# Revit family: SAS-6001_GENERADO
name_source: partatom
category: Equipos mecánicos
revit_build: Autodesk Revit 2014 (Build: 20130308_1515(x64)
units: mm (PartAtom-declared; Revit-internal decimal feet)

## types (10) — shared parameters
Depth = 693 mm  [stored 2.27362 ft]
Fabricante = SAMMIC S.L.
Foodservice Equipment Identifier = Sí
HP = 1.61
Height = 783 mm  [stored 2.5689 ft]
Revision Code = 1
URL = https://www.sammic.com
URL Cutsheet = http://www.sammic.com
Watts = 1200 W
Weight in Pounds = 286.6
Width = 630 mm  [stored 2.06693 ft]

## per-type parameters (varying)
| type | Comentarios de tipo | Cycle | Electric Connection Type | FL Amps | Modelo | Specification by Manufacturer | Volts |
| Cutlery dryer SAS-5001 120/60/1 | Floorstanding flatware polishing machine. | 60 Hz | USA | 10 A | 1370041 | Output: up to 8000 pieces per hour | 120 V |
| Cutlery dryer SAS-5001  230/50/1 | Floorstanding flatware polishing machine. | 50 Hz | EU | 5 A | 1370042 | Output: up to 8000 pieces per hour | 230 V |
| Cutlery dryer SAS-5001  230-400/50/3N | Floorstanding flatware polishing machine.

ELECTRICAL DATA:

230V/50Hz/3~ (5.2A) | 50 Hz |  | 4 A | 1370046 | Output: up to 8000 pieces per hour | 400 V |
| Cutlery dryer SAS-5001 220/60/1 | Floorstanding flatware polishing machine. | 60 Hz | EU | 5 A | 1370049 | Output: up to 8000 pieces per hour | 220 V |
| Cutlery dryer SAS-5001 220-380/60/3N | Floorstanding flatware polishing machine.

ELECTRICAL DATA:

380V/60Hz/3N~ (4.6A) | 60 Hz |  | 5 A | 1370050 | Output: up to 8000 pieces per hour | 220 V |
| Cutlery dryer SAS-6001  230/50/1 | Floorstanding machine with motor brake and outlet fan. | 50 Hz | EU | 5 A | 1370044 | Output: up to 8000 pieces per hour. | 230 V |
| Cutlery dryer SAS-6001 120/60/1 | Floorstanding machine with motor brake and outlet fan. | 60 Hz | USA | 10 A | 1370047 | Output: up to 8000 pieces per hour. | 120 V |
| Cutlery dryer SAS-6001  230-400/50/3N | Floorstanding machine with motor brake and outlet fan.

ELECTRICAL DATA:

230V/50Hz/3~ (5.2A) | 50 Hz |  | 4 A | 1370048 | Output: up to 8000 pieces per hour. | 400 V |
| Cutlery dryer SAS-6001  220/60/1 F | Floorstanding machine with motor brake and outlet fan. | 60 Hz | EU | 5 A | 1370051 | Output: up to 8000 pieces per hour. | 220 V |
| Cutlery dryer-polisher SAS-6001 220-380/60/3N | Floorstanding machine with motor brake and outlet fan.

ELECTRICAL DATA:

380V/60Hz/3N~ (4.6A) | 60 Hz |  | 52 A | 1370052 | Output: up to 8000 pieces per hour. | 220 V |

note: column(s) folded — value = type name in every type: Descripción

note: [stored X ft] marks values corroborated as IEEE doubles in the binary element streams (Revit-internal decimal feet)
